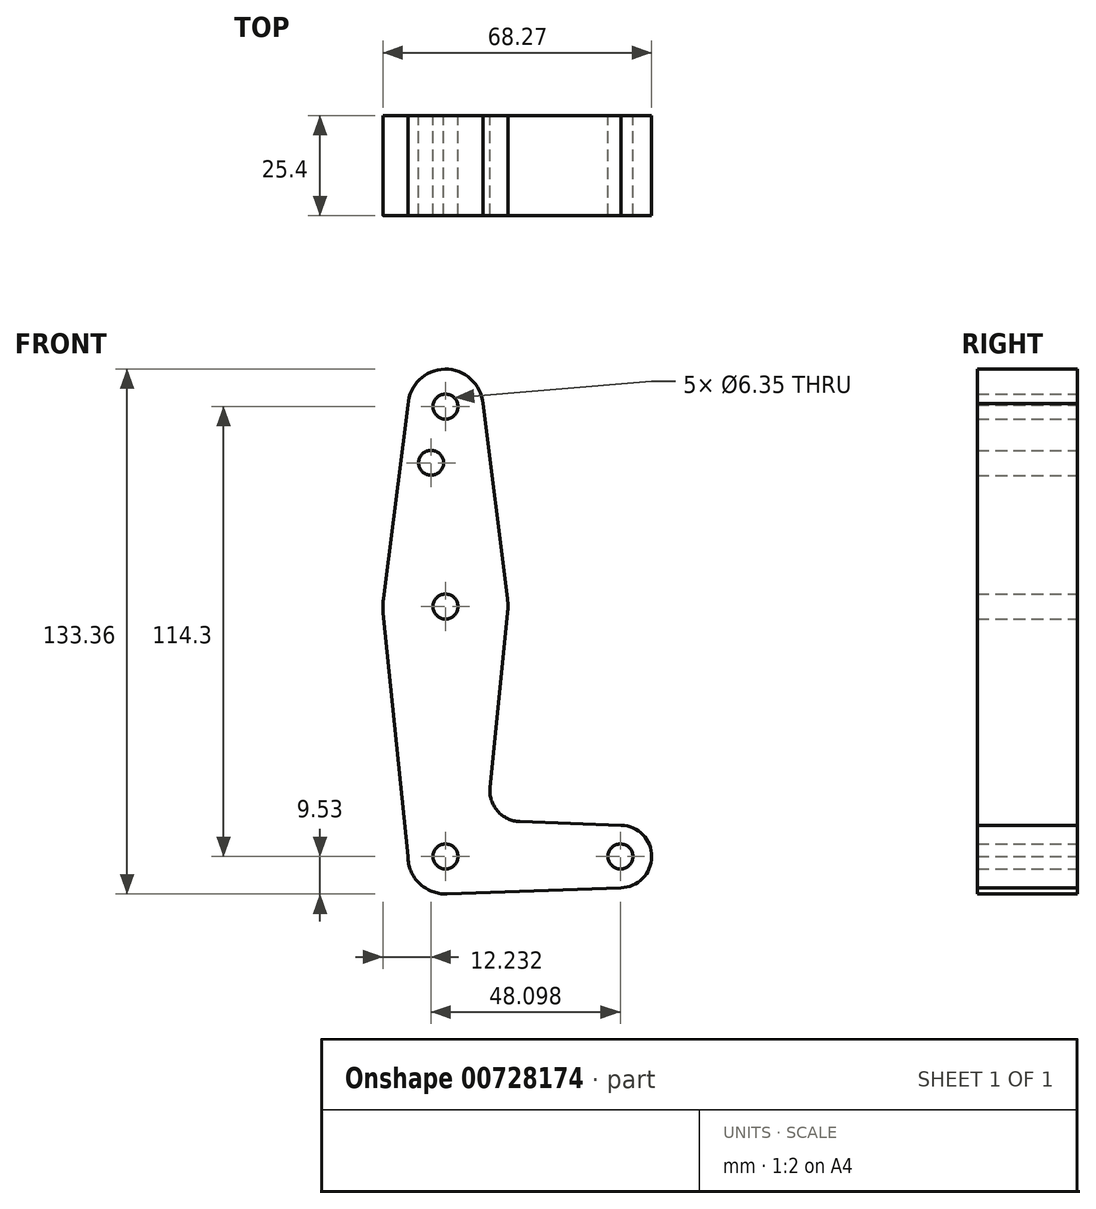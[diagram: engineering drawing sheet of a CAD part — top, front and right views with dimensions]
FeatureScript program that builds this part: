
annotation { "Feature Type Name" : "Feature", "Feature Type Description" : "" }
export const myFeature = defineFeature(function(context is Context, id is Id, definition is map)
    precondition{}
    {
        {
            var Q0;
            Q0=qCreatedBy(makeId("Front.planeOp"),FACE);
            var sketch = newSketch(context, id + "F0", { "sketchPlane" : qUnion([Q0])});
            skLineSegment(sketch, "E0", {"start": v(0, 114.3) * mm, "end": v(0, 0) * mm, "construction": true});
            skLineSegment(sketch, "E1", {"start": v(0, 0) * mm, "end": v(44.45, 0) * mm, "construction": true});
            skCircle(sketch, "E2", {"center": v(0, 114.3) * mm, "radius": 9.53 * mm});
            skCircle(sketch, "E3", {"center": v(44.45, 0) * mm, "radius": 7.94 * mm});
            skCircle(sketch, "E4", {"center": v(0, 0) * mm, "radius": 9.52 * mm});
            skCircle(sketch, "E5", {"center": v(0, 63.5) * mm, "radius": 15.88 * mm});
            skLineSegment(sketch, "E6", {"start": v(44.63, 7.94) * mm, "end": v(18.93, 8.85) * mm});
            skLineSegment(sketch, "E7", {"start": v(44.54, -7.94) * mm, "end": v(0, -9.53) * mm});
            skLineSegment(sketch, "E8", {"start": v(11.3, 17.6) * mm, "end": v(15.8, 61.9) * mm});
            skLineSegment(sketch, "E9", {"start": v(-9.52, 0) * mm, "end": v(-15.8, 61.9) * mm});
            skLineSegment(sketch, "E10", {"start": v(9.5, 115.01) * mm, "end": v(15.75, 65.49) * mm});
            skLineSegment(sketch, "E11", {"start": v(-9.51, 114.74) * mm, "end": v(-15.75, 65.5) * mm});
            skCircle(sketch, "E12", {"center": v(0, 114.3) * mm, "radius": 3.18 * mm});
            skCircle(sketch, "E13", {"center": v(44.45, 0) * mm, "radius": 3.18 * mm});
            skCircle(sketch, "E14", {"center": v(0, 63.5) * mm, "radius": 3.18 * mm});
            skCircle(sketch, "E15", {"center": v(0, 0) * mm, "radius": 3.18 * mm});
            skCircle(sketch, "E16", {"center": v(-3.65, 100.03) * mm, "radius": 3.18 * mm});
            skPoint(sketch, "E17.newPointA", {"position": v(9.52, 0) * mm});
            skArc(sketch, "E17.filletArc", {"start": v(11.3, 17.6) * mm, "mid": v(13.22, 11.57) * mm, "end": v(18.93, 8.85) * mm});
            skSolve(sketch);
        }
        {
            var Q0;
            Q0 = qSketchRegion(id + "FziYpz9JTMPpkCL_0", true);
            var Q1;
            Q1 = qSketchRegion(id + "F0", true);
            extrude(context, id + "F1", {"entities" : qUnion([Q0, Q1]), "depth" : 25.4 * mm, "offsetDistance" : 25.4 * mm});
        }
    });
